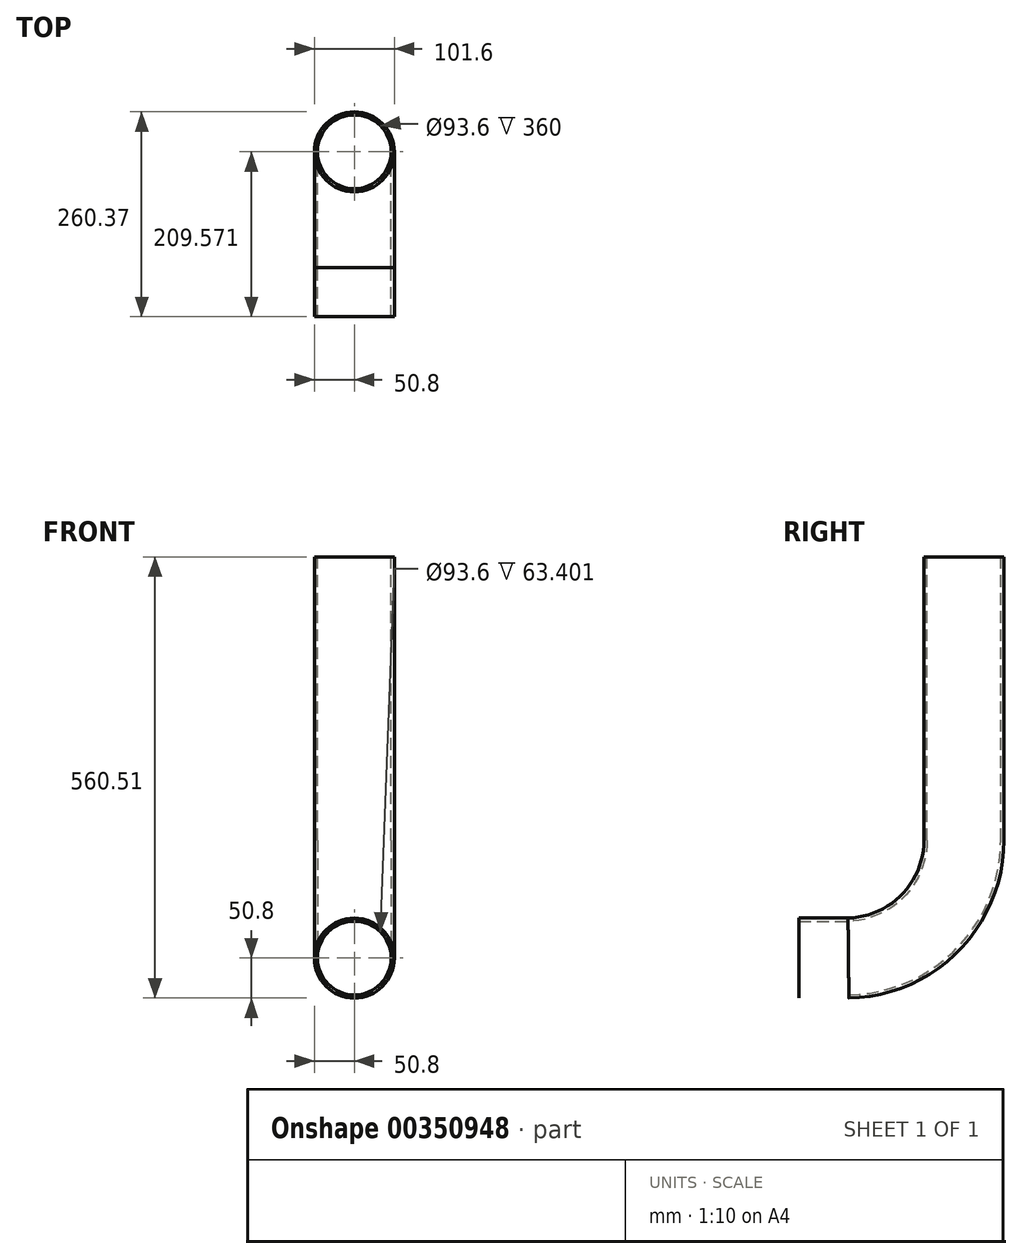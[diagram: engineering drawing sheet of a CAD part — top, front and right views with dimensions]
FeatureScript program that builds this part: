
annotation { "Feature Type Name" : "Feature", "Feature Type Description" : "" }
export const myFeature = defineFeature(function(context is Context, id is Id, definition is map)
    precondition{}
    {
        {
            var Q0;
            Q0=qCreatedBy(makeId("Front.planeOp"),FACE);
            var sketch = newSketch(context, id + "F0", { "sketchPlane" : qUnion([Q0])});
            skCircle(sketch, "E0", {"center": v(0, 0) * mm, "radius": 50.8 * mm});
            skCircle(sketch, "E1", {"center": v(0, 0) * mm, "radius": 46.8 * mm});
            skSolve(sketch);
        }
        {
            var Q0;
            Q0=qCreatedBy(makeId("Right.planeOp"),FACE);
            var sketch = newSketch(context, id + "F1", { "sketchPlane" : qUnion([Q0])});
            skLineSegment(sketch, "E2", {"start": v(0, 0) * mm, "end": v(62.92, 0) * mm});
            skArc(sketch, "E3", {"start": v(62.92, 0) * mm, "mid": v(166.8, 44.92) * mm, "end": v(209.57, 149.7) * mm});
            skLineSegment(sketch, "E4", {"start": v(209.57, 509.7) * mm, "end": v(209.57, 662.07) * mm});
            skLineSegment(sketch, "E5", {"start": v(209.57, 329.7) * mm, "end": v(-31.8, 329.7) * mm});
            skArc(sketch, "E6.MirrorCS", {"start": v(62.92, 659.41) * mm, "mid": v(166.8, 614.5) * mm, "end": v(209.57, 509.7) * mm});
            skLineSegment(sketch, "E7", {"start": v(209.57, 329.7) * mm, "end": v(209.57, 149.7) * mm});
            skLineSegment(sketch, "E8.MirrorCS", {"start": v(209.57, 329.7) * mm, "end": v(209.57, 509.7) * mm});
            skLineSegment(sketch, "E9.MirrorCS", {"start": v(0, 659.41) * mm, "end": v(62.92, 659.41) * mm});
            skSolve(sketch);
        }
        {
            var Q0;
            Q0=makeQuery(id+"F0.imprint","IMPRINT",FACE,{"disambiguationData":[TD([[makeQuery(id+"F0.imprint","IMPRINT",EDGE,{"derivedFrom":sQuery(id+"F0.wireOp",EDGE,"E0")}),1.0]])]});
            var Q1;
            Q1=sQuery(id+"F1.wireOp",EDGE,"E2");
            var Q2;
            Q2=sQuery(id+"F1.wireOp",EDGE,"E3");
            var Q3;
            Q3=sQuery(id+"F1.wireOp",EDGE,"E7");
            var Q4;
            Q4=sQuery(id+"F1.wireOp",EDGE,"E8.MirrorCS");
            sweep(context, id + "F2", {"profiles" : qUnion([Q0]), "path" : qUnion([Q1, Q2, Q3, Q4])});
        }
    });
